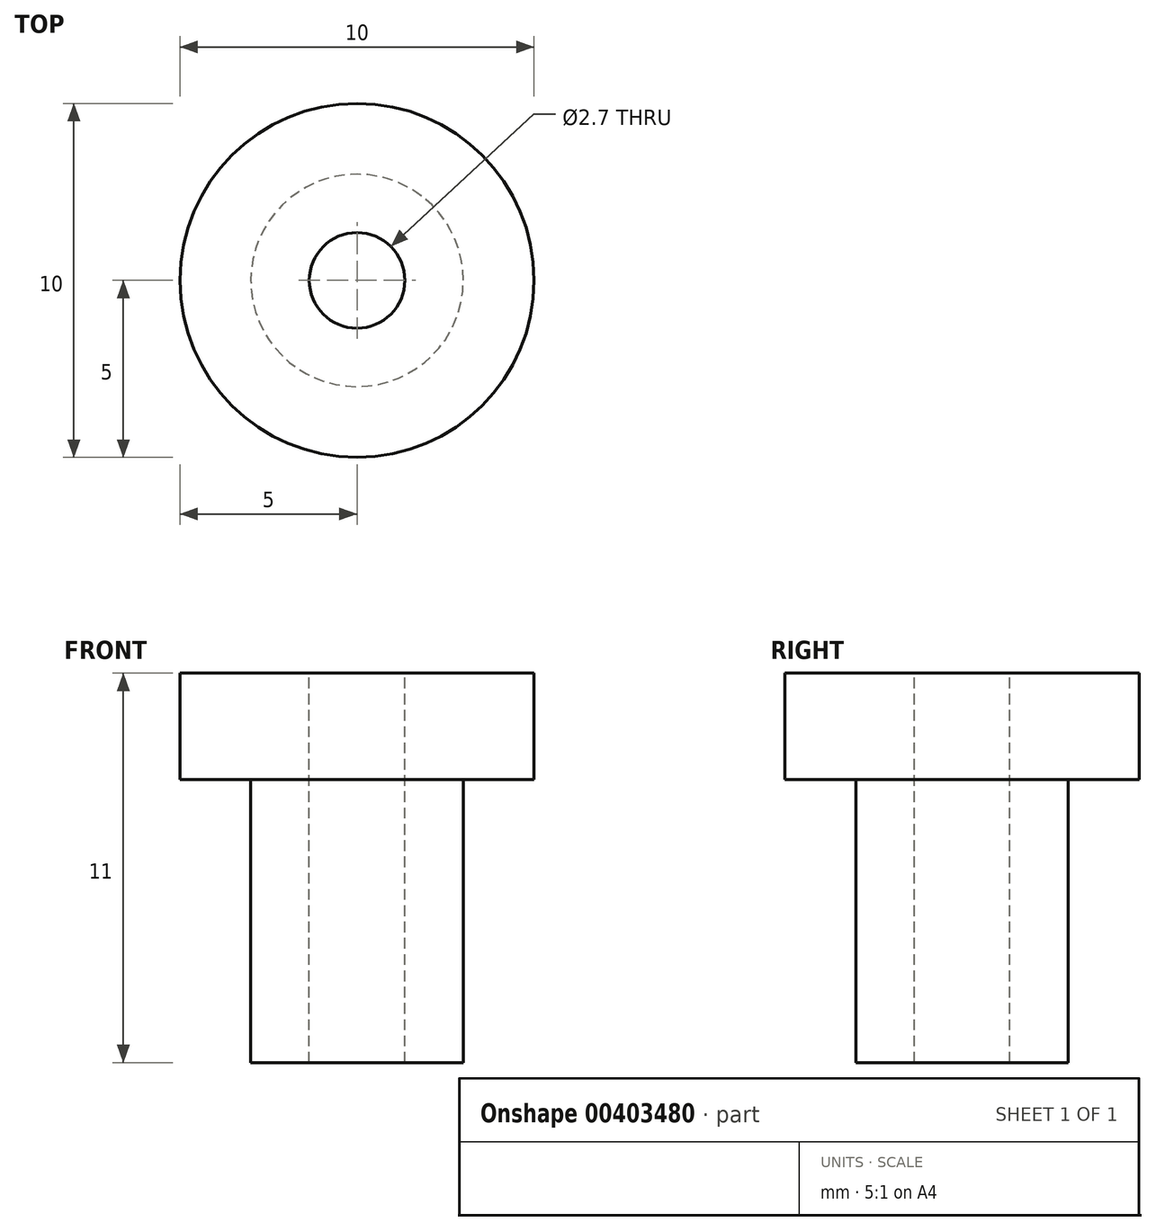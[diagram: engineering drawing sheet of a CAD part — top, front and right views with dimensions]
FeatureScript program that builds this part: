
annotation { "Feature Type Name" : "Feature", "Feature Type Description" : "" }
export const myFeature = defineFeature(function(context is Context, id is Id, definition is map)
    precondition{}
    {
        {
            var Q0;
            Q0=qCreatedBy(makeId("Right.planeOp"),FACE);
            var sketch = newSketch(context, id + "F0", { "sketchPlane" : qUnion([Q0])});
            skLineSegment(sketch, "E0", {"start": v(0, 0) * mm, "end": v(-5, 0) * mm});
            skLineSegment(sketch, "E1", {"start": v(-5, 0) * mm, "end": v(-5, -3) * mm});
            skLineSegment(sketch, "E2", {"start": v(-5, -3) * mm, "end": v(-3, -3) * mm});
            skLineSegment(sketch, "E3", {"start": v(-3, -3) * mm, "end": v(-3, -11) * mm});
            skLineSegment(sketch, "E4", {"start": v(-3, -11) * mm, "end": v(0, -11) * mm});
            skLineSegment(sketch, "E5", {"start": v(0, -11) * mm, "end": v(0, 0) * mm});
            skSolve(sketch);
        }
        {
            var Q0;
            Q0=makeQuery(id+"F0.imprint","IMPRINT",FACE,{"disambiguationData":[TD([[makeQuery(id+"F0.imprint","IMPRINT",EDGE,{"derivedFrom":sQuery(id+"F0.wireOp",EDGE,"E0")}),1.0]])]});
            var Q1;
            Q1=sQuery(id+"F0.wireOp",EDGE,"E5");
            revolve(context, id + "F1", {"entities" : qUnion([Q0]), "axis" : qUnion([Q1]), "revolveType" : RevolveType.FULL});
        }
        {
            var Q0;
            Q0=makeQuery(id+"F1.opRevolve","SWEPT_FACE",FACE,{"disambiguationData":[OSD([sQuery(id+"F0.wireOp",EDGE,"E0")])]});
            var sketch = newSketch(context, id + "F2", { "sketchPlane" : qUnion([Q0])});
            skCircle(sketch, "E6", {"center": v(0, 0) * mm, "radius": 1.35 * mm});
            skSolve(sketch);
        }
        {
            var Q0;
            Q0=makeQuery(id+"F2.imprint","IMPRINT",FACE,{"disambiguationData":[TD([[makeQuery(id+"F2.imprint","IMPRINT",EDGE,{"derivedFrom":sQuery(id+"F2.wireOp",EDGE,"E6")}),1.0]])]});
            extrude(context, id + "F3", {"entities" : qUnion([Q0]), "operationType" : NewBodyOperationType.REMOVE, "oppositeDirection" : true, "depth" : 21.8 * mm});
        }
    });
